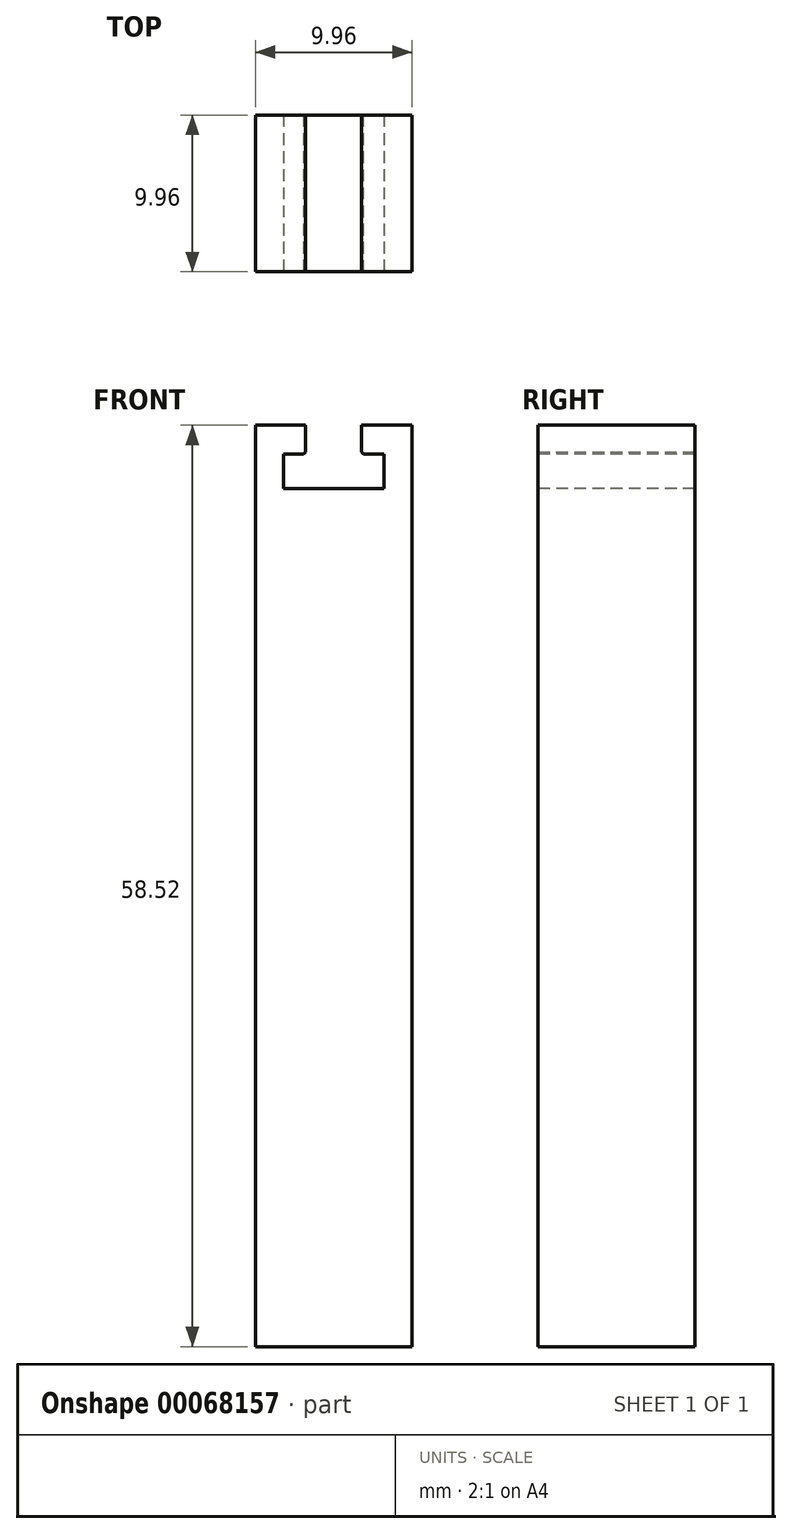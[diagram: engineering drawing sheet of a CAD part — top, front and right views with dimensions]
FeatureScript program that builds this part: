
annotation { "Feature Type Name" : "Feature", "Feature Type Description" : "" }
export const myFeature = defineFeature(function(context is Context, id is Id, definition is map)
    precondition{}
    {
        {
            var Q0;
            Q0=qCreatedBy(makeId("Front.planeOp"),FACE);
            var sketch = newSketch(context, id + "F0", { "sketchPlane" : qUnion([Q0])});
            skLineSegment(sketch, "E0.bottom", {"start": v(0, 0) * mm, "end": v(9.96, 0) * mm});
            skLineSegment(sketch, "E0.top", {"start": v(0, -58.52) * mm, "end": v(9.96, -58.52) * mm});
            skLineSegment(sketch, "E0.left", {"start": v(0, 0) * mm, "end": v(0, -58.52) * mm});
            skLineSegment(sketch, "E0.right", {"start": v(9.96, 0) * mm, "end": v(9.96, -58.52) * mm});
            skSolve(sketch);
        }
        {
            var Q0;
            Q0 = qSketchRegion(id + "F0", true);
            extrude(context, id + "F1", {"entities" : qUnion([Q0]), "oppositeDirection" : true, "depth" : 9.96 * mm});
        }
        {
            var Q0;
            Q0=makeQuery(id+"F1.opExtrude","CAP_FACE",FACE,{"disambiguationData":[OSD([sQuery(id+"F0.wireOp",EDGE,"E0.bottom"),sQuery(id+"F0.wireOp",EDGE,"E0.top"),sQuery(id+"F0.wireOp",EDGE,"E0.left"),sQuery(id+"F0.wireOp",EDGE,"E0.right")])],"isStart":true});
            var sketch = newSketch(context, id + "F2", { "sketchPlane" : qUnion([Q0])});
            skLineSegment(sketch, "E1", {"start": v(3.2, 1.56) * mm, "end": v(3.2, -1.83) * mm});
            skLineSegment(sketch, "E2", {"start": v(3.2, -1.83) * mm, "end": v(1.78, -1.83) * mm});
            skLineSegment(sketch, "E3", {"start": v(1.78, -1.83) * mm, "end": v(1.78, -4.01) * mm});
            skLineSegment(sketch, "E4", {"start": v(1.78, -4.01) * mm, "end": v(8.18, -4.01) * mm});
            skLineSegment(sketch, "E5", {"start": v(8.18, -4.01) * mm, "end": v(8.18, -1.83) * mm});
            skLineSegment(sketch, "E6", {"start": v(8.18, -1.83) * mm, "end": v(6.76, -1.83) * mm});
            skLineSegment(sketch, "E7", {"start": v(6.76, -1.83) * mm, "end": v(6.76, 1.56) * mm});
            skLineSegment(sketch, "E8", {"start": v(6.76, 1.56) * mm, "end": v(3.2, 1.56) * mm});
            skSolve(sketch);
        }
        {
            var Q0;
            Q0 = qSketchRegion(id + "F2", true);
            extrude(context, id + "F3", {"entities" : qUnion([Q0]), "operationType" : NewBodyOperationType.REMOVE, "endBound" : BoundingType.THROUGH_ALL, "oppositeDirection" : true, "depth" : 25.4 * mm});
        }
        {
            var Q0;
            Q0=makeQuery(id+"F3.boolean.opBoolean","COPY",EDGE,{"derivedFrom":makeQuery(id+"F3.opExtrude","SWEPT_EDGE",EDGE,{"disambiguationData":[OSD([sQuery(id+"F2.wireOp",EDGE,"E1"),sQuery(id+"F2.wireOp",EDGE,"E2")])]})});
            var Q1;
            Q1=makeQuery(id+"F3.boolean.opBoolean","COPY",EDGE,{"derivedFrom":makeQuery(id+"F3.opExtrude","SWEPT_EDGE",EDGE,{"disambiguationData":[OSD([sQuery(id+"F2.wireOp",EDGE,"E6"),sQuery(id+"F2.wireOp",EDGE,"E7")])]})});
            chamfer(context, id + "F4", {"entities" : qUnion([Q0, Q1]), "width" : 0.13 * mm, "tangentPropagation" : true});
        }
    });
